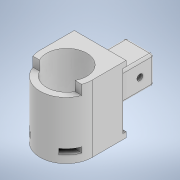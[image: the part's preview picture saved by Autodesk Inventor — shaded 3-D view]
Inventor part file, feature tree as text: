
AUTODESK INVENTOR PART (.ipt)
format: ipt  version: 2020.2 (Build 242310000, 310)  size: 406,016 bytes
history: native  units: mm
features: sketch x10, extrude x7, fillet x4, hole x3
ambient origin geometry x8: Origin, YZ Plane, XZ Plane, XY Plane, X Axis, Y Axis, Z Axis, Center Point
bodies: Solido1 (feature_tree)
feature tree (24):
  extrude  "Estrusione1"  Depth=18.0mm
  extrude  "Estrusione2"  Depth=40.0mm TaperAngle=0.0deg
  extrude  "Estrusione3"  Depth=62.5mm
  extrude  "Estrusione10"  Depth=48.4mm
  hole  "Foro4"  [1 undecoded]
  hole  "Foro5"  [1 undecoded]
  fillet  "Raccordo1"  [1 undecoded]
  fillet  "Raccordo2"  Radius=37.5mm
  fillet  "Raccordo3"  Radius=55.5mm
  extrude  "Estrusione16"  Depth=3.0mm
  hole  "Foro9"  [1 undecoded]
  extrude  "Estrusione17"  Depth=26.0mm
  fillet  "Raccordo5"  Radius=40.0mm
  extrude  "Estrusione18"  Depth=13.0mm
  sketch  "Schizzo1"
  sketch  "Schizzo2"
  sketch  "Schizzo3"
  sketch  "Schizzo14"
  sketch  "Schizzo15"
  sketch  "Schizzo16"
  sketch  "Schizzo26"
  sketch  "Schizzo27"
  sketch  "Schizzo28"
  sketch  "Schizzo29"
note: 4 required parameter values undecoded (feature->parameter linkage not recoverable at this tier; creation-order binding heuristic only, values carry confidence <= 0.55)
